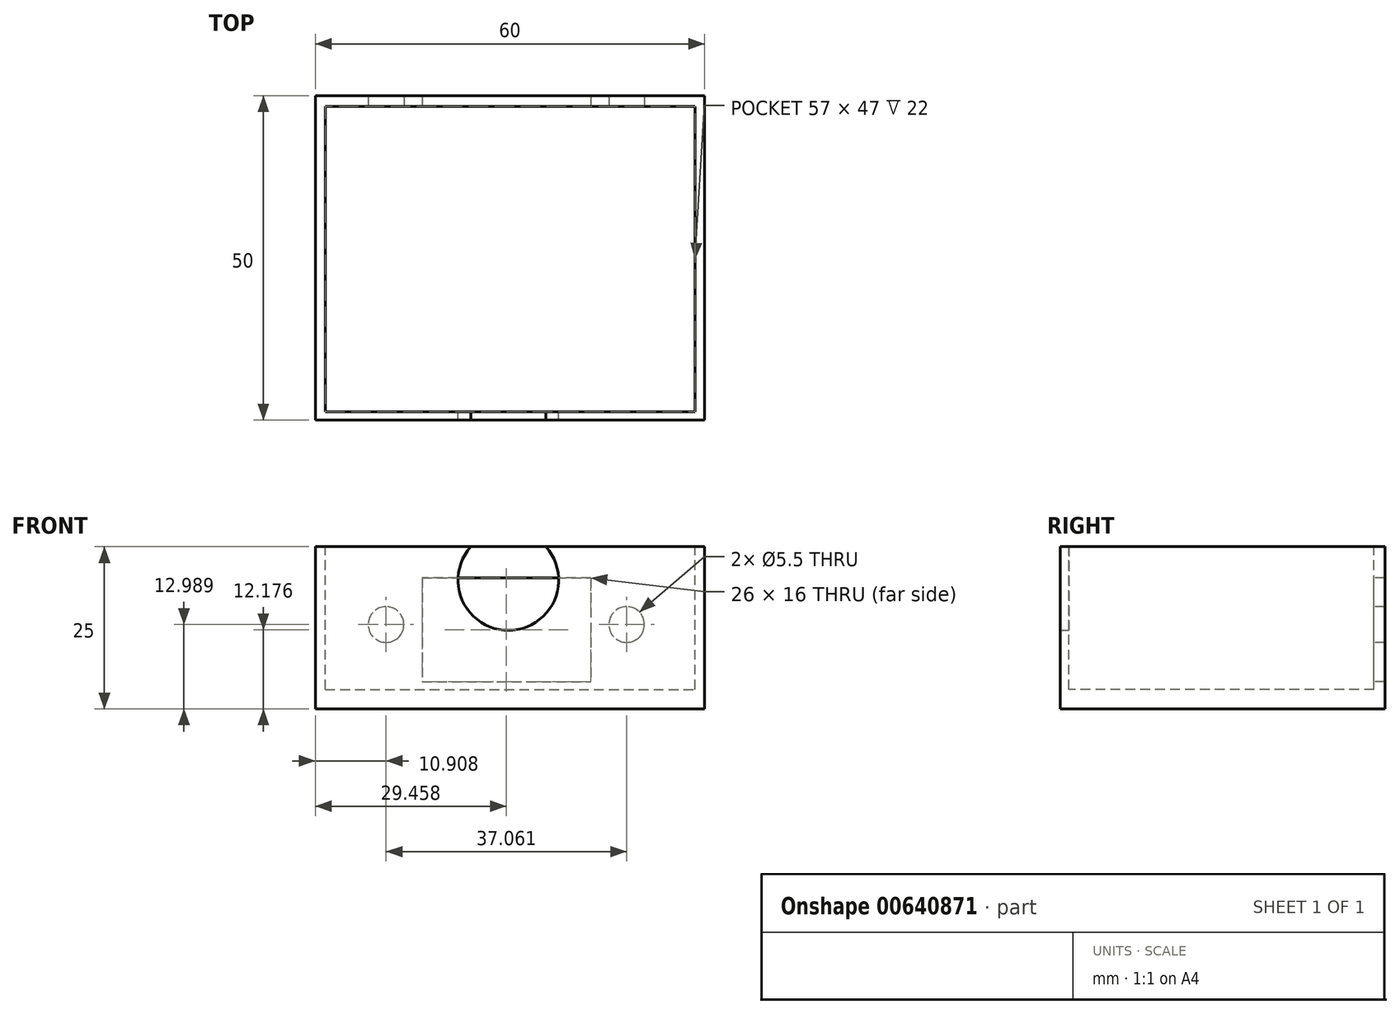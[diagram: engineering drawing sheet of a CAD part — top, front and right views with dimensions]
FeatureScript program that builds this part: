
annotation { "Feature Type Name" : "Feature", "Feature Type Description" : "" }
export const myFeature = defineFeature(function(context is Context, id is Id, definition is map)
    precondition{}
    {
        {
            var Q0;
            Q0=qCreatedBy(makeId("Top.planeOp"),FACE);
            var sketch = newSketch(context, id + "F0", { "sketchPlane" : qUnion([Q0])});
            skLineSegment(sketch, "E0.bottom", {"start": v(-23.36, 25.05) * mm, "end": v(36.64, 25.05) * mm});
            skLineSegment(sketch, "E0.top", {"start": v(-23.36, -24.95) * mm, "end": v(36.64, -24.95) * mm});
            skLineSegment(sketch, "E0.left", {"start": v(-23.36, 25.05) * mm, "end": v(-23.36, -24.95) * mm});
            skLineSegment(sketch, "E0.right", {"start": v(36.64, 25.05) * mm, "end": v(36.64, -24.95) * mm});
            skSolve(sketch);
        }
        {
            var Q0;
            Q0=makeQuery(id+"F0.imprint","IMPRINT",FACE,{"disambiguationData":[TD([[makeQuery(id+"F0.imprint","IMPRINT",EDGE,{"derivedFrom":sQuery(id+"F0.wireOp",EDGE,"E0.bottom")}),-1.0]])]});
            extrude(context, id + "F1", {"entities" : qUnion([Q0]), "depth" : 25 * mm, "offsetDistance" : 25 * mm});
        }
        {
            var Q0;
            Q0=makeQuery(id+"F1.opExtrude","CAP_FACE",FACE,{"disambiguationData":[OSD([sQuery(id+"F0.wireOp",EDGE,"E0.bottom"),sQuery(id+"F0.wireOp",EDGE,"E0.top"),sQuery(id+"F0.wireOp",EDGE,"E0.left"),sQuery(id+"F0.wireOp",EDGE,"E0.right")])],"isStart":false});
            var sketch = newSketch(context, id + "F2", { "sketchPlane" : qUnion([Q0])});
            skLineSegment(sketch, "E1.bottom", {"start": v(-21.82, 23.35) * mm, "end": v(35.18, 23.35) * mm});
            skLineSegment(sketch, "E1.top", {"start": v(-21.82, -23.65) * mm, "end": v(35.18, -23.65) * mm});
            skLineSegment(sketch, "E1.left", {"start": v(-21.82, 23.35) * mm, "end": v(-21.82, -23.65) * mm});
            skLineSegment(sketch, "E1.right", {"start": v(35.18, 23.35) * mm, "end": v(35.18, -23.65) * mm});
            skSolve(sketch);
        }
        {
            var Q0;
            Q0 = qSketchRegion(id + "F2", true);
            extrude(context, id + "F3", {"entities" : qUnion([Q0]), "operationType" : NewBodyOperationType.REMOVE, "oppositeDirection" : true, "depth" : 22 * mm, "offsetDistance" : 25 * mm});
        }
        {
            var Q0;
            Q0=makeQuery(id+"F3.boolean.opBoolean","COPY",FACE,{"derivedFrom":makeQuery(id+"F3.opExtrude","SWEPT_FACE",FACE,{"disambiguationData":[OSD([sQuery(id+"F2.wireOp",EDGE,"E1.bottom")])]})});
            var sketch = newSketch(context, id + "F4", { "sketchPlane" : qUnion([Q0])});
            skLineSegment(sketch, "E2.bottom", {"start": v(19.1, 4.18) * mm, "end": v(-6.9, 4.18) * mm});
            skLineSegment(sketch, "E2.top", {"start": v(19.1, 20.18) * mm, "end": v(-6.9, 20.18) * mm});
            skLineSegment(sketch, "E2.left", {"start": v(19.1, 4.18) * mm, "end": v(19.1, 20.18) * mm});
            skLineSegment(sketch, "E2.right", {"start": v(-6.9, 4.18) * mm, "end": v(-6.9, 20.18) * mm});
            skPoint(sketch, "E2.middle", {"position": v(6.1, 12.18) * mm});
            skSolve(sketch);
        }
        {
            var Q0;
            Q0 = qSketchRegion(id + "F4", true);
            extrude(context, id + "F5", {"entities" : qUnion([Q0]), "operationType" : NewBodyOperationType.REMOVE, "endBound" : BoundingType.THROUGH_ALL, "oppositeDirection" : true, "depth" : 5 * mm, "offsetDistance" : 25 * mm});
        }
        {
            var Q0;
            Q0=makeQuery(id+"F3.boolean.opBoolean","COPY",FACE,{"derivedFrom":makeQuery(id+"F3.opExtrude","SWEPT_FACE",FACE,{"disambiguationData":[OSD([sQuery(id+"F2.wireOp",EDGE,"E1.bottom")])]})});
            var sketch = newSketch(context, id + "F6", { "sketchPlane" : qUnion([Q0])});
            skPoint(sketch, "E3", {"position": v(-12.45, 12.99) * mm});
            skPoint(sketch, "E4", {"position": v(24.6, 12.99) * mm});
            skSolve(sketch);
        }
        {
            var Q0;
            Q0=sQuery(id+"F6.wireOp",VERTEX,"E3");
            var Q1;
            Q1=makeQuery(id+"F1.opExtrude","SWEPT_BODY",BODY,{"disambiguationData":[OSD([sQuery(id+"F0.wireOp",EDGE,"E0.bottom"),sQuery(id+"F0.wireOp",EDGE,"E0.top"),sQuery(id+"F0.wireOp",EDGE,"E0.left"),sQuery(id+"F0.wireOp",EDGE,"E0.right")])]});
            hole(context, id + "F7", {"style" : HoleStyle.SIMPLE, "endStyle" : HoleEndStyle.THROUGH, "standardTappedOrClearance" : lookupTablePath({ "standard" : "ISO", "fit" : "Normal", "size" : "M5", "type" : "Clearance" }), "standardBlindInLast" : lookupTablePath({ "fit" : "Standard", "standard" : "ISO", "size" : "M5", "type" : "Clearance" }), "holeDiameter" : 5.5 * mm, "majorDiameter" : 5 * mm, "isTappedThrough" : true, "tappedDepth" : 12 * mm, "tapClearance" : 3, "locations" : qUnion([Q0]), "scope" : qUnion([Q1])});
        }
        {
            var Q0;
            Q0=sQuery(id+"F6.wireOp",VERTEX,"E4");
            var Q1;
            Q1=makeQuery(id+"F1.opExtrude","SWEPT_BODY",BODY,{"disambiguationData":[OSD([sQuery(id+"F0.wireOp",EDGE,"E0.bottom"),sQuery(id+"F0.wireOp",EDGE,"E0.top"),sQuery(id+"F0.wireOp",EDGE,"E0.left"),sQuery(id+"F0.wireOp",EDGE,"E0.right")])]});
            hole(context, id + "F8", {"style" : HoleStyle.SIMPLE, "endStyle" : HoleEndStyle.THROUGH, "standardTappedOrClearance" : lookupTablePath({ "standard" : "ISO", "fit" : "Normal", "size" : "M5", "type" : "Clearance" }), "standardBlindInLast" : lookupTablePath({ "fit" : "Standard", "standard" : "ISO", "size" : "M5", "type" : "Clearance" }), "holeDiameter" : 5.5 * mm, "majorDiameter" : 5 * mm, "isTappedThrough" : true, "tappedDepth" : 12 * mm, "tapClearance" : 3, "locations" : qUnion([Q0]), "scope" : qUnion([Q1])});
        }
        {
            var Q0;
            Q0=makeQuery(id+"F3.boolean.opBoolean","COPY",FACE,{"derivedFrom":makeQuery(id+"F3.opExtrude","SWEPT_FACE",FACE,{"disambiguationData":[OSD([sQuery(id+"F2.wireOp",EDGE,"E1.top")])]})});
            var sketch = newSketch(context, id + "F9", { "sketchPlane" : qUnion([Q0])});
            skPoint(sketch, "E5", {"position": v(-6.39, 19.84) * mm});
            skSolve(sketch);
        }
        {
            var Q0;
            Q0=sQuery(id+"F9.wireOp",VERTEX,"E5");
            var Q1;
            Q1=makeQuery(id+"F1.opExtrude","SWEPT_BODY",BODY,{"disambiguationData":[OSD([sQuery(id+"F0.wireOp",EDGE,"E0.bottom"),sQuery(id+"F0.wireOp",EDGE,"E0.top"),sQuery(id+"F0.wireOp",EDGE,"E0.left"),sQuery(id+"F0.wireOp",EDGE,"E0.right")])]});
            hole(context, id + "F10", {"style" : HoleStyle.SIMPLE, "endStyle" : HoleEndStyle.THROUGH, "standardTappedOrClearance" : lookupTablePath({ "standard" : "ISO", "fit" : "Normal", "size" : "M14", "type" : "Clearance" }), "standardBlindInLast" : lookupTablePath({ "fit" : "Standard", "standard" : "ISO", "size" : "M14", "type" : "Clearance" }), "holeDiameter" : 15.5 * mm, "majorDiameter" : 5 * mm, "isTappedThrough" : true, "tappedDepth" : 12 * mm, "tapClearance" : 3, "locations" : qUnion([Q0]), "scope" : qUnion([Q1])});
        }
    });
